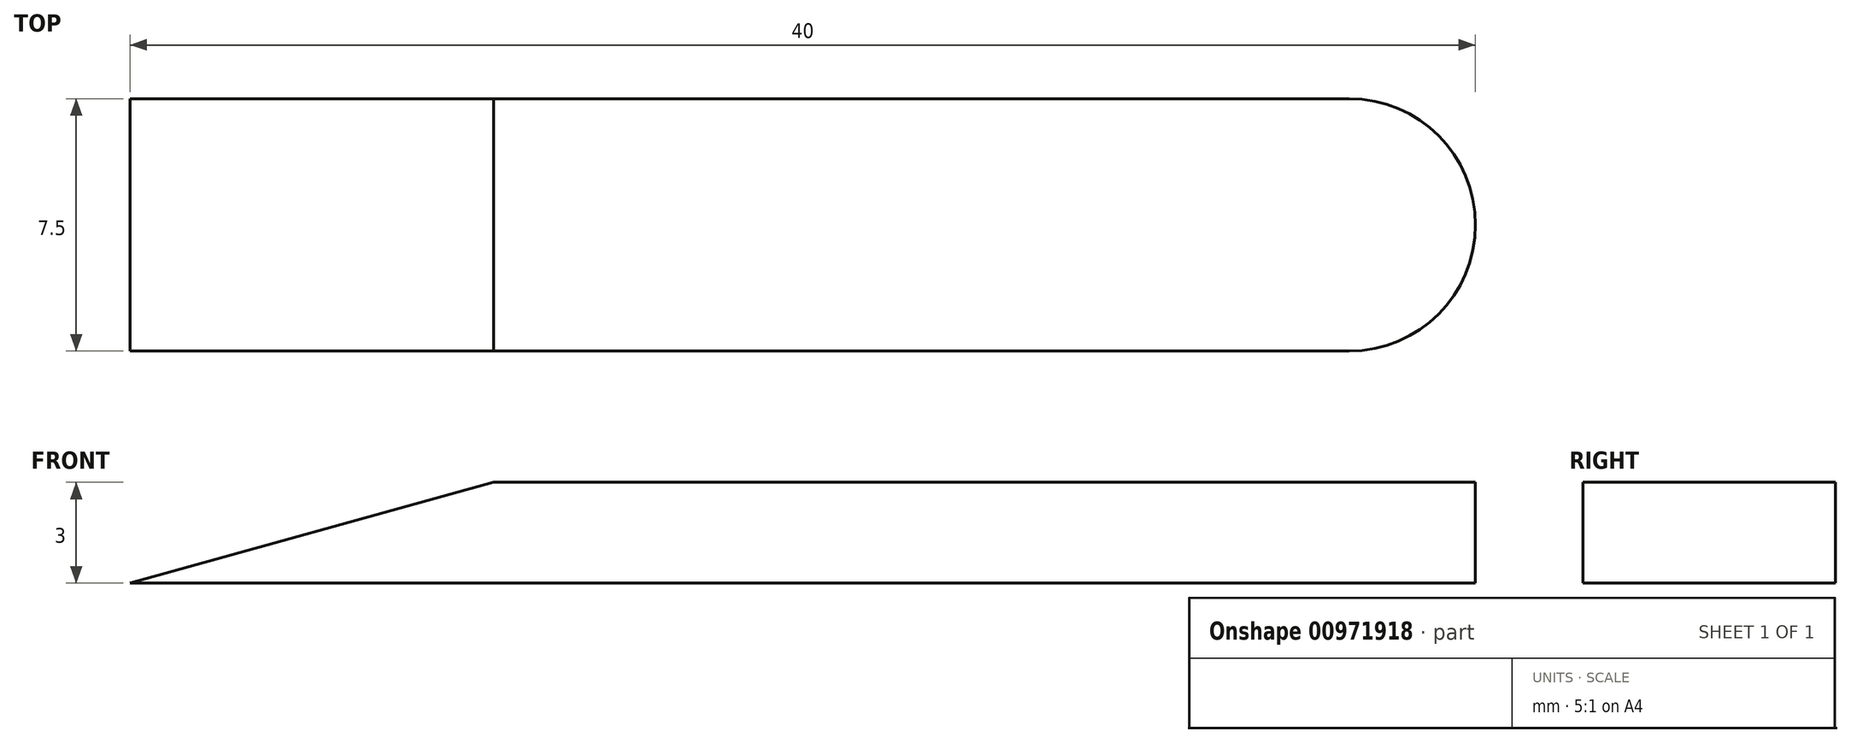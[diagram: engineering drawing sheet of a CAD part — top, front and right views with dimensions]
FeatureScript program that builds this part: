
annotation { "Feature Type Name" : "Feature", "Feature Type Description" : "" }
export const myFeature = defineFeature(function(context is Context, id is Id, definition is map)
    precondition{}
    {
        {
            var Q0;
            Q0=qCreatedBy(makeId("Top.planeOp"),FACE);
            var sketch = newSketch(context, id + "F0", { "sketchPlane" : qUnion([Q0])});
            skLineSegment(sketch, "E0.bottom", {"start": v(0, 0) * mm, "end": v(-40, 0) * mm});
            skLineSegment(sketch, "E0.top", {"start": v(0, -7.5) * mm, "end": v(-40, -7.5) * mm});
            skLineSegment(sketch, "E0.left", {"start": v(0, 0) * mm, "end": v(0, -7.5) * mm});
            skLineSegment(sketch, "E0.right", {"start": v(-40, 0) * mm, "end": v(-40, -7.5) * mm});
            skSolve(sketch);
        }
        {
            var Q0;
            Q0=makeQuery(id+"F0.imprint","IMPRINT",FACE,{"disambiguationData":[TD([[makeQuery(id+"F0.imprint","IMPRINT",EDGE,{"derivedFrom":sQuery(id+"F0.wireOp",EDGE,"E0.bottom")}),1.0]])]});
            extrude(context, id + "F1", {"entities" : qUnion([Q0]), "depth" : 3 * mm, "offsetDistance" : 25 * mm});
        }
        {
            var Q0;
            Q0=makeQuery(id+"F1.opExtrude","SWEPT_FACE",FACE,{"disambiguationData":[OSD([sQuery(id+"F0.wireOp",EDGE,"E0.top")])]});
            var sketch = newSketch(context, id + "F2", { "sketchPlane" : qUnion([Q0])});
            skLineSegment(sketch, "E1", {"start": v(-40, 0) * mm, "end": v(-29.2, 3) * mm});
            skSolve(sketch);
        }
        {
            var Q0;
            {var subQ0=sQuery(id+"F2.wireOp",EDGE,"E1");Q0=makeQuery(id+"F2.imprint","IMPRINT",FACE,{"disambiguationData":[TD([[makeQuery(id+"F2.imprint","IMPRINT",EDGE,{"derivedFrom":subQ0}),1.0]])]});}
            extrude(context, id + "F3", {"entities" : qUnion([Q0]), "operationType" : NewBodyOperationType.REMOVE, "oppositeDirection" : true, "depth" : 10 * mm, "offsetDistance" : 25 * mm});
        }
        {
            var Q0;
            Q0=makeQuery(id+"F1.opExtrude","CAP_FACE",FACE,{"disambiguationData":[OSD([sQuery(id+"F0.wireOp",EDGE,"E0.bottom"),sQuery(id+"F0.wireOp",EDGE,"E0.top"),sQuery(id+"F0.wireOp",EDGE,"E0.left"),sQuery(id+"F0.wireOp",EDGE,"E0.right")])],"isStart":false});
            var sketch = newSketch(context, id + "F4", { "sketchPlane" : qUnion([Q0])});
            skLineSegment(sketch, "E2", {"start": v(0, -3.75) * mm, "end": v(-11.16, -3.75) * mm, "construction": true});
            skLineSegment(sketch, "E3", {"start": v(-3.75, -2.68) * mm, "end": v(-3.75, -4.88) * mm, "construction": true});
            skCircle(sketch, "E4", {"center": v(-3.75, -3.75) * mm, "radius": 3.75 * mm});
            skSolve(sketch);
        }
        {
            var Q0;
            {var subQ0=sQuery(id+"F4.wireOp",EDGE,"E4");var subQ1=makeQuery(id+"F1.opExtrude","CAP_EDGE",EDGE,{"disambiguationData":[OSD([sQuery(id+"F0.wireOp",EDGE,"E0.bottom")])],"isStart":false});var subQ2=makeQuery(id+"F4.imprint","INTERSECT",VERTEX,{"derivedFrom":[subQ1,subQ0]});Q0=makeQuery(id+"F4.imprint","IMPRINT",FACE,{"disambiguationData":[TD([[makeQuery(id+"F4.imprint","IMPRINT",EDGE,{"disambiguationData":[TD([[subQ2,1.0]])],"derivedFrom":subQ0}),-1.0]])]});}
            var Q1;
            {var subQ0=sQuery(id+"F4.wireOp",EDGE,"E4");var subQ1=makeQuery(id+"F1.opExtrude","CAP_EDGE",EDGE,{"disambiguationData":[OSD([sQuery(id+"F0.wireOp",EDGE,"E0.left")])],"isStart":false});var subQ2=makeQuery(id+"F4.imprint","INTERSECT",VERTEX,{"derivedFrom":[subQ1,subQ0]});Q1=makeQuery(id+"F4.imprint","IMPRINT",FACE,{"disambiguationData":[TD([[makeQuery(id+"F4.imprint","IMPRINT",EDGE,{"disambiguationData":[TD([[subQ2,1.0]])],"derivedFrom":subQ0}),-1.0]])]});}
            extrude(context, id + "F5", {"entities" : qUnion([Q0, Q1]), "operationType" : NewBodyOperationType.REMOVE, "oppositeDirection" : true, "depth" : 3 * mm, "offsetDistance" : 25 * mm});
        }
    });
